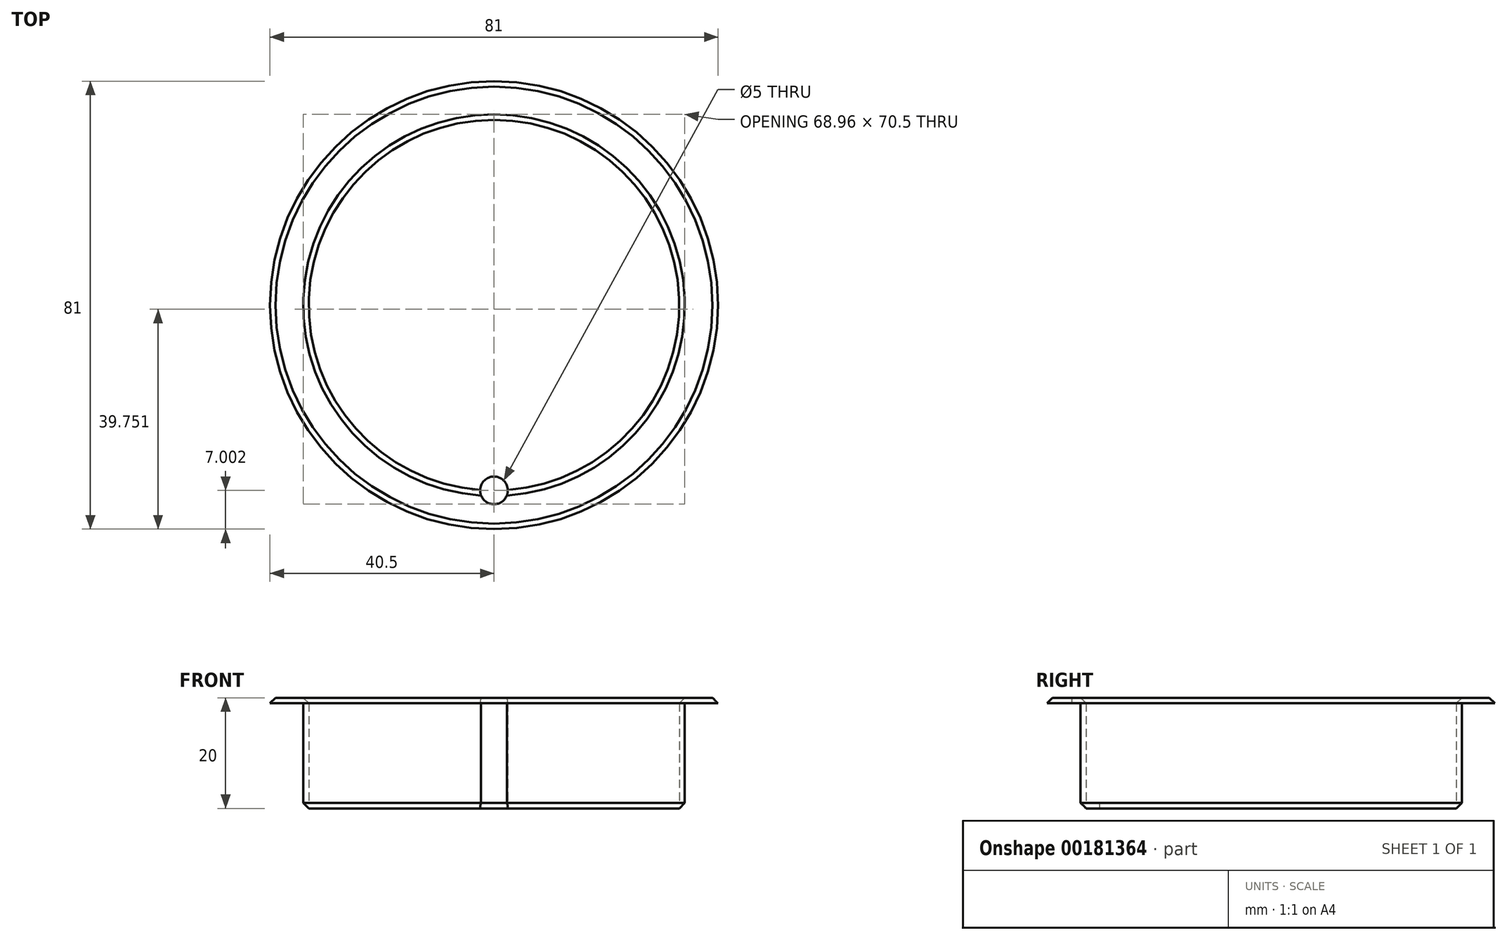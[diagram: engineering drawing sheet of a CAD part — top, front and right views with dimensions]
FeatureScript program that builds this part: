
annotation { "Feature Type Name" : "Feature", "Feature Type Description" : "" }
export const myFeature = defineFeature(function(context is Context, id is Id, definition is map)
    precondition{}
    {
        {
            var Q0;
            Q0=qCreatedBy(makeId("Top.planeOp"),FACE);
            var sketch = newSketch(context, id + "F0", { "sketchPlane" : qUnion([Q0])});
            skCircle(sketch, "E0", {"center": v(0, 0) * mm, "radius": 34.5 * mm});
            skSolve(sketch);
        }
        {
            var Q0;
            Q0 = qSketchRegion(id + "F0", true);
            extrude(context, id + "F1", {"entities" : qUnion([Q0]), "depth" : 1 * mm});
        }
        {
            var Q0;
            Q0=makeQuery(id+"F1.opExtrude","CAP_FACE",FACE,{"disambiguationData":[OSD([sQuery(id+"F0.wireOp",EDGE,"E0")])],"isStart":false});
            var sketch = newSketch(context, id + "F2", { "sketchPlane" : qUnion([Q0])});
            skCircle(sketch, "E1.0", {"center": v(0, 0) * mm, "radius": 33.5 * mm});
            skSolve(sketch);
        }
        {
            var Q0;
            Q0=makeQuery(id+"F2.imprint","IMPRINT",FACE,{"disambiguationData":[TD([[makeQuery(id+"F2.imprint","IMPRINT",EDGE,{"derivedFrom":sQuery(id+"F2.wireOp",EDGE,"E1.0")}),-1.0]])]});
            extrude(context, id + "F3", {"entities" : qUnion([Q0]), "operationType" : NewBodyOperationType.ADD, "depth" : 18 * mm});
        }
        {
            var Q0;
            Q0=makeQuery(id+"F3.opExtrude","CAP_FACE",FACE,{"disambiguationData":[OSD([sQuery(id+"F0.wireOp",EDGE,"E0"),sQuery(id+"F2.wireOp",EDGE,"E1.0")])],"isStart":false});
            var sketch = newSketch(context, id + "F4", { "sketchPlane" : qUnion([Q0])});
            skCircle(sketch, "E2.0", {"center": v(0, 0) * mm, "radius": 40.5 * mm});
            skSolve(sketch);
        }
        {
            var Q0;
            Q0=makeQuery(id+"F4.imprint","IMPRINT",FACE,{"disambiguationData":[TD([[makeQuery(id+"F4.imprint","IMPRINT",EDGE,{"derivedFrom":sQuery(id+"F4.wireOp",EDGE,"E2.0")}),1.0]])]});
            var Q1;
            Q1=makeQuery(id+"F4.imprint","IMPRINT",FACE,{"disambiguationData":[TD([[makeQuery(id+"F4.imprint","IMPRINT",EDGE,{"derivedFrom":makeQuery(id+"F3.opExtrude","CAP_EDGE",EDGE,{"disambiguationData":[OSD([sQuery(id+"F2.wireOp",EDGE,"E1.0")])],"isStart":false})}),-1.0]])]});
            extrude(context, id + "F5", {"entities" : qUnion([Q0, Q1]), "operationType" : NewBodyOperationType.ADD, "depth" : 1 * mm});
        }
        {
            var Q0;
            Q0=makeQuery(id+"F3.opExtrude","CAP_EDGE",EDGE,{"disambiguationData":[OSD([sQuery(id+"F2.wireOp",EDGE,"E1.0")])],"isStart":true});
            var Q1;
            Q1=makeQuery(id+"F1.opExtrude","CAP_FACE",FACE,{"disambiguationData":[OSD([sQuery(id+"F0.wireOp",EDGE,"E0")])],"isStart":true});
            var Q2;
            Q2=makeQuery(id+"F5.opExtrude","CAP_EDGE",EDGE,{"disambiguationData":[OSD([sQuery(id+"F2.wireOp",EDGE,"E1.0")])],"isStart":false});
            var Q3;
            Q3=makeQuery(id+"F5.opExtrude","CAP_FACE",FACE,{"disambiguationData":[OSD([sQuery(id+"F2.wireOp",EDGE,"E1.0"),sQuery(id+"F4.wireOp",EDGE,"E2.0")])],"isStart":false});
            chamfer(context, id + "F6", {"entities" : qUnion([Q0, Q1, Q2, Q3]), "width" : 1 * mm, "tangentPropagation" : true});
        }
        {
            var Q0;
            Q0=qCreatedBy(makeId("Top.planeOp"),FACE);
            var sketch = newSketch(context, id + "F7", { "sketchPlane" : qUnion([Q0])});
            skCircle(sketch, "E3", {"center": v(0, -33.5) * mm, "radius": 2.5 * mm});
            skSolve(sketch);
        }
        {
            var Q0;
            Q0 = qSketchRegion(id + "F7", true);
            extrude(context, id + "F8", {"entities" : qUnion([Q0]), "depth" : 25 * mm});
        }
        {
            var Q0;
            Q0=makeQuery(id+"F8.opExtrude","SWEPT_BODY",BODY,{"disambiguationData":[OSD([sQuery(id+"F7.wireOp",EDGE,"E3")])]});
            var Q1;
            Q1=makeQuery(id+"F1.opExtrude","SWEPT_BODY",BODY,{"disambiguationData":[OSD([sQuery(id+"F0.wireOp",EDGE,"E0")])]});
            booleanBodies(context, id + "F9", {"operationType" : BooleanOperationType.SUBTRACTION, "tools" : qUnion([Q0]), "targets" : qUnion([Q1])});
        }
    });
